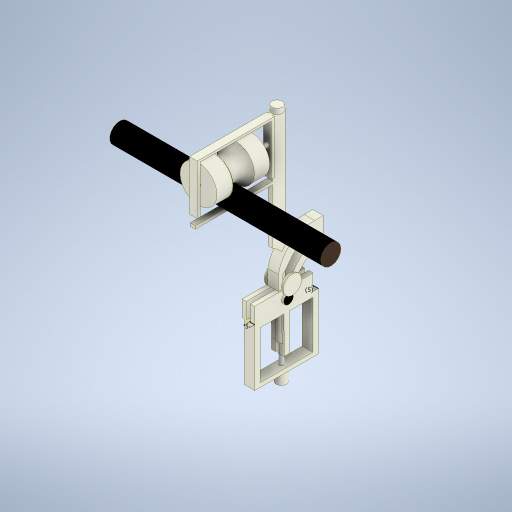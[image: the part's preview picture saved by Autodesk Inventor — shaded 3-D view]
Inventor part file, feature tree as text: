
AUTODESK INVENTOR PART (.ipt)
format: ipt  version: 2024 (Build 280153000, 153)  size: 642,048 bytes
history: native  units: in
note: dims shown in document units (in); Inventor stores cm internally (conversion verified against a paired STEP export)
features: sketch x35, extrude x27, plane x5, mirror x3, revolve x1
ambient origin geometry x8: Origin, YZ Plane, XZ Plane, XY Plane, X Axis, Y Axis, Z Axis, Center Point
bodies: Solid1 (feature_tree)
feature tree (71):
  sketch  "Sketch1"  dims[d7=0.3937in d8=0.0in d9=0.1575in]
  extrude  "Extrusion1"  Depth=0.1575in
  sketch  "Sketch3"  dims[d13=0.3937in d14=0.0in d15=0.315in]
  extrude  "Extrusion2"  Depth=0.1969in
  extrude  "Extrusion3"  Depth=0.315in
  extrude  "Extrusion4"  Depth=0.1969in
  extrude  "Extrusion5"  Depth=0.1575in TaperAngle=0.0deg
  sketch  "Sketch8"  dims[d30=3.937in d31=0.3937in d32=0.0in]
  sketch  "Sketch9"  dims[d33=0.3937in d34=0.0in d35=0.0787in d36=0.0in]
  sketch  "Sketch10"  dims[d37=0.0787in d38=0.0in d39=0.0787in d40=0.0in]
  plane  "Work Plane1"
  plane  "Work Plane2"
  mirror  "Mirror1"
  extrude  "Extrusion6"  Depth=0.1969in
  extrude  "Extrusion7"  Depth=0.0787in
  extrude  "Extrusion8"  Depth=0.3937in TaperAngle=0.0deg
  extrude  "Extrusion9"  Depth=0.0787in TaperAngle=0.0deg
  extrude  "Extrusion10"  Depth=0.0787in TaperAngle=0.0deg
  extrude  "Extrusion11"  Depth=0.4724in
  extrude  "Extrusion12"  Depth=0.3937in
  extrude  "Extrusion13"  Depth=0.1181in TaperAngle=0.0deg
  extrude  "Extrusion14"  Depth=1.9685in
  sketch  "Sketch20"  dims[d68=0.0787in d69=0.0in d70=7.874in d71=0.0in]
  extrude  "Extrusion15"  Depth=0.5906in
  plane  "Work Plane3"
  extrude  "Extrusion16"  Depth=0.5906in TaperAngle=0.0deg
  plane  "Work Plane4"
  extrude  "Extrusion17"  Depth=0.5906in TaperAngle=0.0deg
  plane  "Work Plane5"
  revolve  "Revolution1"  Angle=90.0deg
  extrude  "Extrusion18"  Depth=0.1969in TaperAngle=0.0deg
  extrude  "Extrusion19"  Depth=0.0787in TaperAngle=0.0deg
  extrude  "Extrusion20"  Depth=0.3937in TaperAngle=0.0deg
  mirror  "Mirror2"
  extrude  "Extrusion21"  Depth=0.3937in TaperAngle=0.0deg
  extrude  "Extrusion22"  Depth=0.0787in TaperAngle=0.0deg
  sketch  "Sketch30"
  extrude  "Extrusion23"  [1 undecoded]
  extrude  "Extrusion24"  [1 undecoded]
  extrude  "Extrusion25"  [1 undecoded]
  extrude  "Extrusion26"  [1 undecoded]
  extrude  "Extrusion27"  [1 undecoded]
  mirror  "Mirror3"
  sketch  "Sketch2"  dims[d10=0.3937in d11=0.0in d12=0.1969in]
  sketch  "Sketch4"  dims[d16=1.1811in d17=0.0in d22=0.1969in]
  sketch  "Sketch5"  dims[d23=0.1575in d24=0.1575in d25=0.0in]
  sketch  "Sketch6"  dims[d26=0.1969in d27=0.1969in]
  sketch  "Sketch7"  dims[d28=0.1969in d29=0.0787in]
  sketch  "Sketch11"  dims[d41=0.4724in d42=4.7244in]
  sketch  "Sketch12"  dims[d43=0.1575in d44=0.0in d45=0.3937in]
  sketch  "Sketch13"  dims[d46=0.1969in d47=0.0in d48=0.1181in d49=0.0in]
  sketch  "Sketch14"  dims[d50=2.7559in d51=0.0in d52=1.9685in]
  sketch  "Sketch15"  dims[d53=2.7559in d54=0.0in d55=0.5906in]
  sketch  "Sketch16"  dims[d56=1.378in d57=0.5906in d58=0.0in]
  sketch  "Sketch17"  dims[d59=0.7874in d60=0.5906in d61=0.0in]
  sketch  "Sketch18"  dims[d62=-0.1378in d63=90.0deg]
  sketch  "Sketch19"  dims[d64=1.7717in d65=0.0in d66=0.1969in d67=0.0in]
  sketch  "Sketch21"  dims[d72=0.3937in d73=0.3937in d74=0.0in]
  sketch  "Sketch22"  dims[d75=0.3937in d76=0.0in d77=0.3937in d78=0.0in]
  sketch  "Sketch23"  dims[d79=0.0787in d80=0.0in d81=0.0787in d82=0.0in]
  sketch  "Sketch24"  dims[d83=0.0394in d84=0.0in]
  sketch  "Sketch25"
  sketch  "Sketch26"
  sketch  "Sketch27"
  sketch  "Sketch28"
  sketch  "Sketch29"
  sketch  "Sketch31"
  sketch  "Sketch32"
  sketch  "Sketch33"
  sketch  "Sketch34"
  sketch  "Sketch35"
note: 5 required parameter values undecoded (feature->parameter linkage not recoverable at this tier; creation-order binding heuristic only, values carry confidence <= 0.55)
